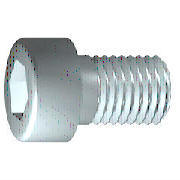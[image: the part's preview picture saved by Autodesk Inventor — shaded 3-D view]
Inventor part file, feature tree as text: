
AUTODESK INVENTOR PART (.ipt)
format: ipt  version: 2022 (Build 260153000, 153)  size: 195,584 bytes
history: native  units: mm (DEFAULTED — no unit token found)
features: sketch x2, extrude x1, plane x1, fillet x1
ambient origin geometry x7: Origin, YZ Plane, XY Plane, X Axis, Y Axis, Z Axis, Center Point
bodies: Solid1 (feature_tree), Body (feature_tree)
feature tree (5):
  extrude  "Slot"  Depth=4.0mm
  plane  "Work Plane1"
  fillet  "Fillet2"  Radius=4.0mm
  sketch  "Sketch1"  dims[d1=10.25mm d2=0.429515mm d3=4.0mm]
  sketch  "Sketch2"  dims[d4=2.0mm d5=60.0deg d6=4.0mm d7=4.0mm d8=3.464102mm d9=7.0mm d10=90.0deg d11=10.0mm d12=0.0mm d13=10.25mm d14=0.0mm d15=0.429415mm d16=0.429415mm d17=0.4mm d19=0.0mm d26=12.0mm d27=45.0deg d28=0.0mm d29=0.0mm d30=0.1mm]
